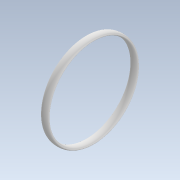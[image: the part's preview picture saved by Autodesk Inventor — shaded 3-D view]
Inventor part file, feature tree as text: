
AUTODESK INVENTOR PART (.ipt)
format: ipt  version: 2021 (Build 250183000, 183)  size: 206,848 bytes
history: native  units: mm
features: other x4, reference x3, revolve x1, sketch x1
ambient origin geometry x8: Origin, YZ Plane, XZ Plane, XY Plane, X Axis, Y Axis, Z Axis, Center Point
bodies: Body1 (feature_tree)
feature tree (9):
  other  "Sólido1"
  revolve  "Revolución1"  [1 undecoded]
  sketch  "Boceto1"  dims[d0=28.0mm d1=20.0mm d2=295.0mm d3=90.0deg d4=3.0mm]
  reference  "Referencia1"
  reference  "Referencia2"
  reference  "Referencia3"
  parser-record x1  (decoder bookkeeping rows leaked as tree rows — omitted from the tree; the rows remain in map.json)
  other  "Ensamble_Llanta.iam"
  other  "cubierta:1"
note: 1 file-system path scrubbed to <path> (originals preserved in map.json)
note: 1 required parameter value undecoded (feature->parameter linkage not recoverable at this tier; creation-order binding heuristic only, values carry confidence <= 0.55)
